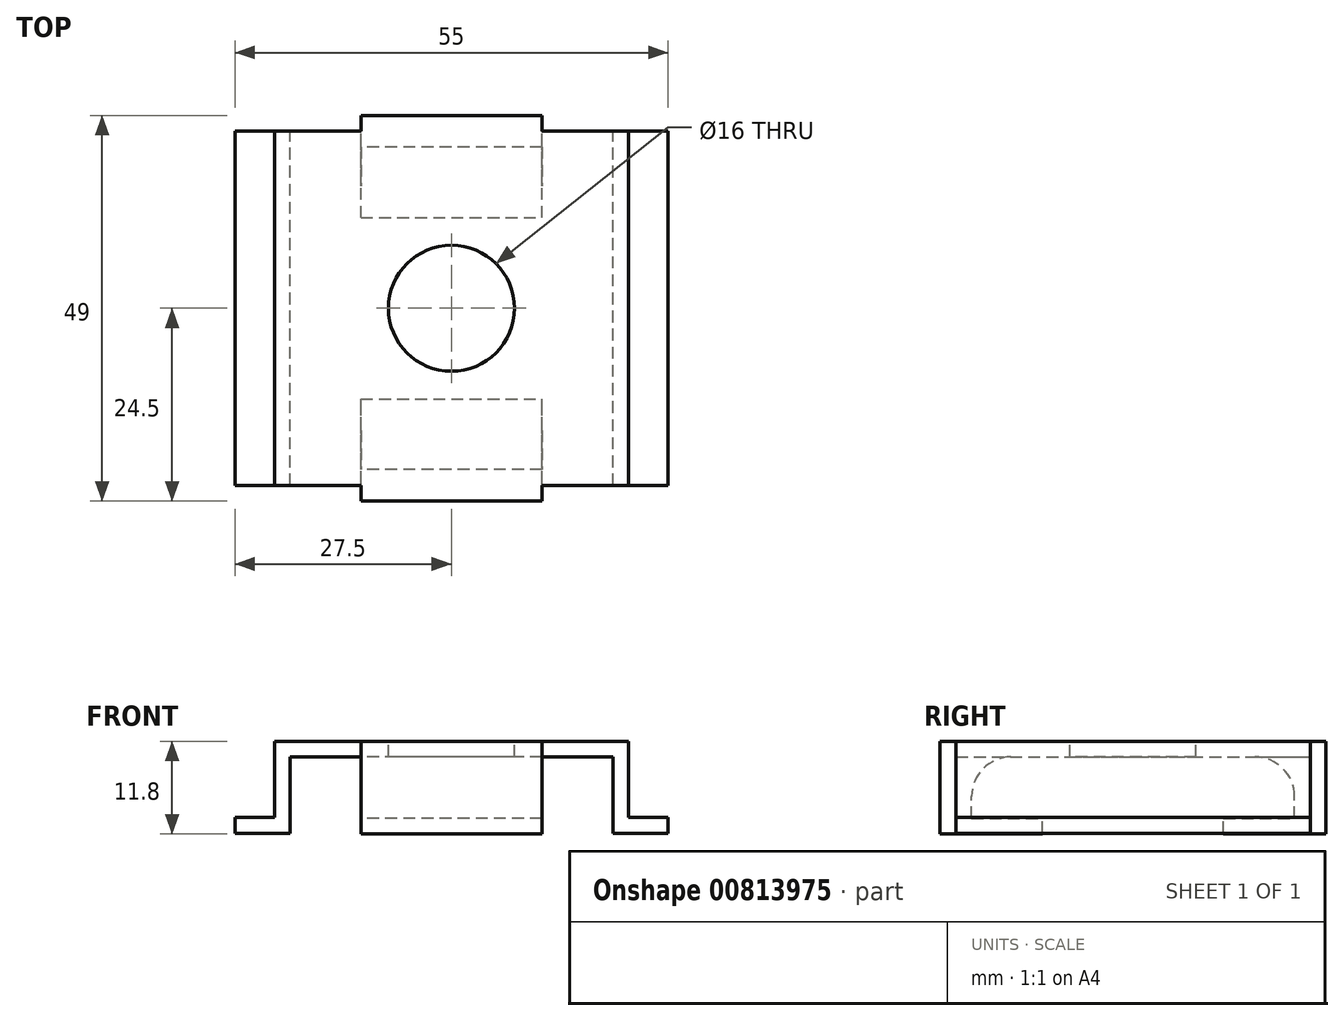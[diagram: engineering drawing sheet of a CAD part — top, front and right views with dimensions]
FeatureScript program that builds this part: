
annotation { "Feature Type Name" : "Feature", "Feature Type Description" : "" }
export const myFeature = defineFeature(function(context is Context, id is Id, definition is map)
    precondition{}
    {
        {
            var Q0;
            Q0=qCreatedBy(makeId("Top.planeOp"),FACE);
            var sketch = newSketch(context, id + "F0", { "sketchPlane" : qUnion([Q0])});
            skLineSegment(sketch, "E0.bottom", {"start": v(22.5, -22.5) * mm, "end": v(-22.5, -22.5) * mm});
            skLineSegment(sketch, "E0.top", {"start": v(22.5, 22.5) * mm, "end": v(-22.5, 22.5) * mm});
            skLineSegment(sketch, "E0.left", {"start": v(22.5, -22.5) * mm, "end": v(22.5, 22.5) * mm});
            skLineSegment(sketch, "E0.right", {"start": v(-22.5, -22.5) * mm, "end": v(-22.5, 22.5) * mm});
            skPoint(sketch, "E0.middle", {"position": v(0, 0) * mm});
            skSolve(sketch);
        }
        {
            var Q0;
            Q0=makeQuery(id+"F0.imprint","IMPRINT",FACE,{"disambiguationData":[TD([[makeQuery(id+"F0.imprint","IMPRINT",EDGE,{"derivedFrom":sQuery(id+"F0.wireOp",EDGE,"E0.bottom")}),-1.0]])]});
            extrude(context, id + "F1", {"entities" : qUnion([Q0]), "depth" : 2 * mm, "offsetDistance" : 25 * mm});
        }
        {
            var Q0;
            Q0=makeQuery(id+"F1.opExtrude","CAP_FACE",FACE,{"disambiguationData":[OSD([sQuery(id+"F0.wireOp",EDGE,"E0.bottom"),sQuery(id+"F0.wireOp",EDGE,"E0.top"),sQuery(id+"F0.wireOp",EDGE,"E0.left"),sQuery(id+"F0.wireOp",EDGE,"E0.right")])],"isStart":false});
            var sketch = newSketch(context, id + "F2", { "sketchPlane" : qUnion([Q0])});
            skCircle(sketch, "E1", {"center": v(0, 0) * mm, "radius": 8 * mm});
            skSolve(sketch);
        }
        {
            var Q0;
            Q0=makeQuery(id+"F2.imprint","IMPRINT",FACE,{"disambiguationData":[TD([[makeQuery(id+"F2.imprint","IMPRINT",EDGE,{"derivedFrom":sQuery(id+"F2.wireOp",EDGE,"E1")}),1.0]])]});
            extrude(context, id + "F3", {"entities" : qUnion([Q0]), "operationType" : NewBodyOperationType.REMOVE, "oppositeDirection" : true, "depth" : 25 * mm, "offsetDistance" : 25 * mm});
        }
        {
            var Q0;
            Q0=makeQuery(id+"F1.opExtrude","CAP_FACE",FACE,{"disambiguationData":[OSD([sQuery(id+"F0.wireOp",EDGE,"E0.bottom"),sQuery(id+"F0.wireOp",EDGE,"E0.top"),sQuery(id+"F0.wireOp",EDGE,"E0.left"),sQuery(id+"F0.wireOp",EDGE,"E0.right")])],"isStart":false});
            var sketch = newSketch(context, id + "F4", { "sketchPlane" : qUnion([Q0])});
            skLineSegment(sketch, "E2.bottom", {"start": v(11.5, 20.5) * mm, "end": v(-11.5, 20.5) * mm});
            skLineSegment(sketch, "E2.top", {"start": v(11.5, 24.5) * mm, "end": v(-11.5, 24.5) * mm});
            skLineSegment(sketch, "E2.left", {"start": v(11.5, 20.5) * mm, "end": v(11.5, 24.5) * mm});
            skLineSegment(sketch, "E2.right", {"start": v(-11.5, 20.5) * mm, "end": v(-11.5, 24.5) * mm});
            skPoint(sketch, "E2.middle", {"position": v(0, 22.5) * mm});
            skLineSegment(sketch, "E3.bottom", {"start": v(11.5, -24.5) * mm, "end": v(-11.5, -24.5) * mm});
            skLineSegment(sketch, "E3.top", {"start": v(11.5, -20.5) * mm, "end": v(-11.5, -20.5) * mm});
            skLineSegment(sketch, "E3.left", {"start": v(11.5, -24.5) * mm, "end": v(11.5, -20.5) * mm});
            skLineSegment(sketch, "E3.right", {"start": v(-11.5, -24.5) * mm, "end": v(-11.5, -20.5) * mm});
            skPoint(sketch, "E3.middle", {"position": v(0, -22.5) * mm});
            skSolve(sketch);
        }
        {
            var Q0;
            Q0 = qSketchRegion(id + "F4", true);
            extrude(context, id + "F5", {"entities" : qUnion([Q0]), "operationType" : NewBodyOperationType.ADD, "oppositeDirection" : true, "depth" : 9.8 * mm, "offsetDistance" : 25 * mm});
        }
        {
            var Q0;
            Q0=makeQuery(id+"F5.opExtrude","CAP_FACE",FACE,{"disambiguationData":[OSD([sQuery(id+"F4.wireOp",EDGE,"E3.bottom"),sQuery(id+"F4.wireOp",EDGE,"E3.top"),sQuery(id+"F4.wireOp",EDGE,"E3.left"),sQuery(id+"F4.wireOp",EDGE,"E3.right")])],"isStart":false});
            var sketch = newSketch(context, id + "F6", { "sketchPlane" : qUnion([Q0])});
            skLineSegment(sketch, "E4.bottom", {"start": v(-11.5, 24.5) * mm, "end": v(11.5, 24.5) * mm});
            skLineSegment(sketch, "E4.top", {"start": v(-11.5, 11.5) * mm, "end": v(11.5, 11.5) * mm});
            skLineSegment(sketch, "E4.left", {"start": v(-11.5, 24.5) * mm, "end": v(-11.5, 11.5) * mm});
            skLineSegment(sketch, "E4.right", {"start": v(11.5, 24.5) * mm, "end": v(11.5, 11.5) * mm});
            skSolve(sketch);
        }
        {
            var Q0;
            {var subQ0=sQuery(id+"F6.wireOp",EDGE,"E4.top");Q0=makeQuery(id+"F6.imprint","IMPRINT",FACE,{"disambiguationData":[TD([[makeQuery(id+"F6.imprint","IMPRINT",EDGE,{"derivedFrom":subQ0}),1.0]])]});}
            var Q1;
            {var subQ0=sQuery(id+"F6.wireOp",EDGE,"E4.bottom");Q1=makeQuery(id+"F6.imprint","IMPRINT",FACE,{"disambiguationData":[TD([[makeQuery(id+"F6.imprint","IMPRINT",EDGE,{"derivedFrom":subQ0}),1.0]])]});}
            extrude(context, id + "F7", {"entities" : qUnion([Q0, Q1]), "operationType" : NewBodyOperationType.ADD, "depth" : 2 * mm, "offsetDistance" : 25 * mm});
        }
        {
            var Q0;
            Q0=makeQuery(id+"F5.opExtrude","CAP_FACE",FACE,{"disambiguationData":[OSD([sQuery(id+"F4.wireOp",EDGE,"E2.bottom"),sQuery(id+"F4.wireOp",EDGE,"E2.top"),sQuery(id+"F4.wireOp",EDGE,"E2.left"),sQuery(id+"F4.wireOp",EDGE,"E2.right")])],"isStart":false});
            var sketch = newSketch(context, id + "F8", { "sketchPlane" : qUnion([Q0])});
            skLineSegment(sketch, "E5.bottom", {"start": v(-11.5, -24.5) * mm, "end": v(11.5, -24.5) * mm});
            skLineSegment(sketch, "E5.top", {"start": v(-11.5, -11.5) * mm, "end": v(11.5, -11.5) * mm});
            skLineSegment(sketch, "E5.left", {"start": v(-11.5, -24.5) * mm, "end": v(-11.5, -11.5) * mm});
            skLineSegment(sketch, "E5.right", {"start": v(11.5, -24.5) * mm, "end": v(11.5, -11.5) * mm});
            skSolve(sketch);
        }
        {
            var Q0;
            Q0 = qSketchRegion(id + "F8", true);
            extrude(context, id + "F9", {"entities" : qUnion([Q0]), "operationType" : NewBodyOperationType.ADD, "depth" : 2 * mm, "offsetDistance" : 25 * mm});
        }
        {
            var Q0;
            Q0=makeQuery(id+"F1.opExtrude","CAP_FACE",FACE,{"disambiguationData":[OSD([sQuery(id+"F0.wireOp",EDGE,"E0.bottom"),sQuery(id+"F0.wireOp",EDGE,"E0.top"),sQuery(id+"F0.wireOp",EDGE,"E0.left"),sQuery(id+"F0.wireOp",EDGE,"E0.right")])],"isStart":true});
            var sketch = newSketch(context, id + "F10", { "sketchPlane" : qUnion([Q0])});
            skLineSegment(sketch, "E6.bottom", {"start": v(-22.5, 22.5) * mm, "end": v(-20.5, 22.5) * mm});
            skLineSegment(sketch, "E6.top", {"start": v(-22.5, -22.5) * mm, "end": v(-20.5, -22.5) * mm});
            skLineSegment(sketch, "E6.left", {"start": v(-22.5, 22.5) * mm, "end": v(-22.5, -22.5) * mm});
            skLineSegment(sketch, "E6.right", {"start": v(-20.5, 22.5) * mm, "end": v(-20.5, -22.5) * mm});
            skLineSegment(sketch, "E7.bottom", {"start": v(22.5, 22.5) * mm, "end": v(20.5, 22.5) * mm});
            skLineSegment(sketch, "E7.top", {"start": v(22.5, -22.5) * mm, "end": v(20.5, -22.5) * mm});
            skLineSegment(sketch, "E7.left", {"start": v(22.5, 22.5) * mm, "end": v(22.5, -22.5) * mm});
            skLineSegment(sketch, "E7.right", {"start": v(20.5, 22.5) * mm, "end": v(20.5, -22.5) * mm});
            skSolve(sketch);
        }
        {
            var Q0;
            Q0 = qSketchRegion(id + "F10", true);
            extrude(context, id + "F11", {"entities" : qUnion([Q0]), "operationType" : NewBodyOperationType.ADD, "depth" : 7.7 * mm, "offsetDistance" : 25 * mm});
        }
        {
            var Q0;
            Q0=makeQuery(id+"F11.opExtrude","CAP_FACE",FACE,{"disambiguationData":[OSD([sQuery(id+"F10.wireOp",EDGE,"E6.bottom"),sQuery(id+"F10.wireOp",EDGE,"E6.top"),sQuery(id+"F10.wireOp",EDGE,"E6.left"),sQuery(id+"F10.wireOp",EDGE,"E6.right")])],"isStart":false});
            var sketch = newSketch(context, id + "F12", { "sketchPlane" : qUnion([Q0])});
            skLineSegment(sketch, "E8.bottom", {"start": v(-20.5, 22.5) * mm, "end": v(-27.5, 22.5) * mm});
            skLineSegment(sketch, "E8.top", {"start": v(-20.5, -22.5) * mm, "end": v(-27.5, -22.5) * mm});
            skLineSegment(sketch, "E8.left", {"start": v(-20.5, 22.5) * mm, "end": v(-20.5, -22.5) * mm});
            skLineSegment(sketch, "E8.right", {"start": v(-27.5, 22.5) * mm, "end": v(-27.5, -22.5) * mm});
            skSolve(sketch);
        }
        {
            var Q0;
            Q0=makeQuery(id+"F11.opExtrude","CAP_FACE",FACE,{"disambiguationData":[OSD([sQuery(id+"F10.wireOp",EDGE,"E7.bottom"),sQuery(id+"F10.wireOp",EDGE,"E7.top"),sQuery(id+"F10.wireOp",EDGE,"E7.left"),sQuery(id+"F10.wireOp",EDGE,"E7.right")])],"isStart":false});
            var sketch = newSketch(context, id + "F13", { "sketchPlane" : qUnion([Q0])});
            skLineSegment(sketch, "E9.bottom", {"start": v(20.5, 22.5) * mm, "end": v(27.5, 22.5) * mm});
            skLineSegment(sketch, "E9.top", {"start": v(20.5, -22.5) * mm, "end": v(27.5, -22.5) * mm});
            skLineSegment(sketch, "E9.left", {"start": v(20.5, 22.5) * mm, "end": v(20.5, -22.5) * mm});
            skLineSegment(sketch, "E9.right", {"start": v(27.5, 22.5) * mm, "end": v(27.5, -22.5) * mm});
            skSolve(sketch);
        }
        {
            var Q0;
            Q0 = qSketchRegion(id + "F12", true);
            var Q1;
            Q1 = qSketchRegion(id + "F13", true);
            extrude(context, id + "F14", {"entities" : qUnion([Q0, Q1]), "operationType" : NewBodyOperationType.ADD, "depth" : 2 * mm, "offsetDistance" : 25 * mm});
        }
        {
            var Q0;
            Q0=makeQuery(id+"F5.opExtrude","CAP_EDGE",EDGE,{"disambiguationData":[OSD([sQuery(id+"F4.wireOp",EDGE,"E3.top")])],"isStart":false});
            var Q1;
            Q1=makeQuery(id+"F5.opExtrude","CAP_EDGE",EDGE,{"disambiguationData":[OSD([sQuery(id+"F4.wireOp",EDGE,"E2.bottom")])],"isStart":false});
            var Q2;
            Q2=makeQuery(id+"F5.boolean.opBoolean","INTERSECT",EDGE,{"derivedFrom":[makeQuery(id+"F1.opExtrude","CAP_FACE",FACE,{"disambiguationData":[OSD([sQuery(id+"F0.wireOp",EDGE,"E0.bottom"),sQuery(id+"F0.wireOp",EDGE,"E0.top"),sQuery(id+"F0.wireOp",EDGE,"E0.left"),sQuery(id+"F0.wireOp",EDGE,"E0.right")])],"isStart":true}),makeQuery(id+"F5.opExtrude","SWEPT_FACE",FACE,{"disambiguationData":[OSD([sQuery(id+"F4.wireOp",EDGE,"E2.bottom")])]})]});
            var Q3;
            Q3=makeQuery(id+"F5.boolean.opBoolean","INTERSECT",EDGE,{"derivedFrom":[makeQuery(id+"F1.opExtrude","CAP_FACE",FACE,{"disambiguationData":[OSD([sQuery(id+"F0.wireOp",EDGE,"E0.bottom"),sQuery(id+"F0.wireOp",EDGE,"E0.top"),sQuery(id+"F0.wireOp",EDGE,"E0.left"),sQuery(id+"F0.wireOp",EDGE,"E0.right")])],"isStart":true}),makeQuery(id+"F5.opExtrude","SWEPT_FACE",FACE,{"disambiguationData":[OSD([sQuery(id+"F4.wireOp",EDGE,"E3.top")])]})]});
            var Q4;
            Q4=makeQuery(id+"F11.opExtrude","CAP_EDGE",EDGE,{"disambiguationData":[OSD([sQuery(id+"F10.wireOp",EDGE,"E7.right")])],"isStart":true});
            var Q5;
            Q5=makeQuery(id+"F11.opExtrude","CAP_EDGE",EDGE,{"disambiguationData":[OSD([sQuery(id+"F10.wireOp",EDGE,"E6.right")])],"isStart":true});
            var Q6;
            Q6=makeQuery(id+"F11.opExtrude","CAP_EDGE",EDGE,{"disambiguationData":[OSD([sQuery(id+"F10.wireOp",EDGE,"E6.left")])],"isStart":false});
            var Q7;
            Q7=makeQuery(id+"F11.opExtrude","CAP_EDGE",EDGE,{"disambiguationData":[OSD([sQuery(id+"F10.wireOp",EDGE,"E7.left")])],"isStart":false});
            fillet(context, id + "F15", {"entities" : qUnion([Q0, Q1, Q2, Q3, Q4, Q5, Q6, Q7]), "radius" : 5 * mm, "tangentPropagation" : true, "allowEdgeOverflow" : false});
        }
    });
